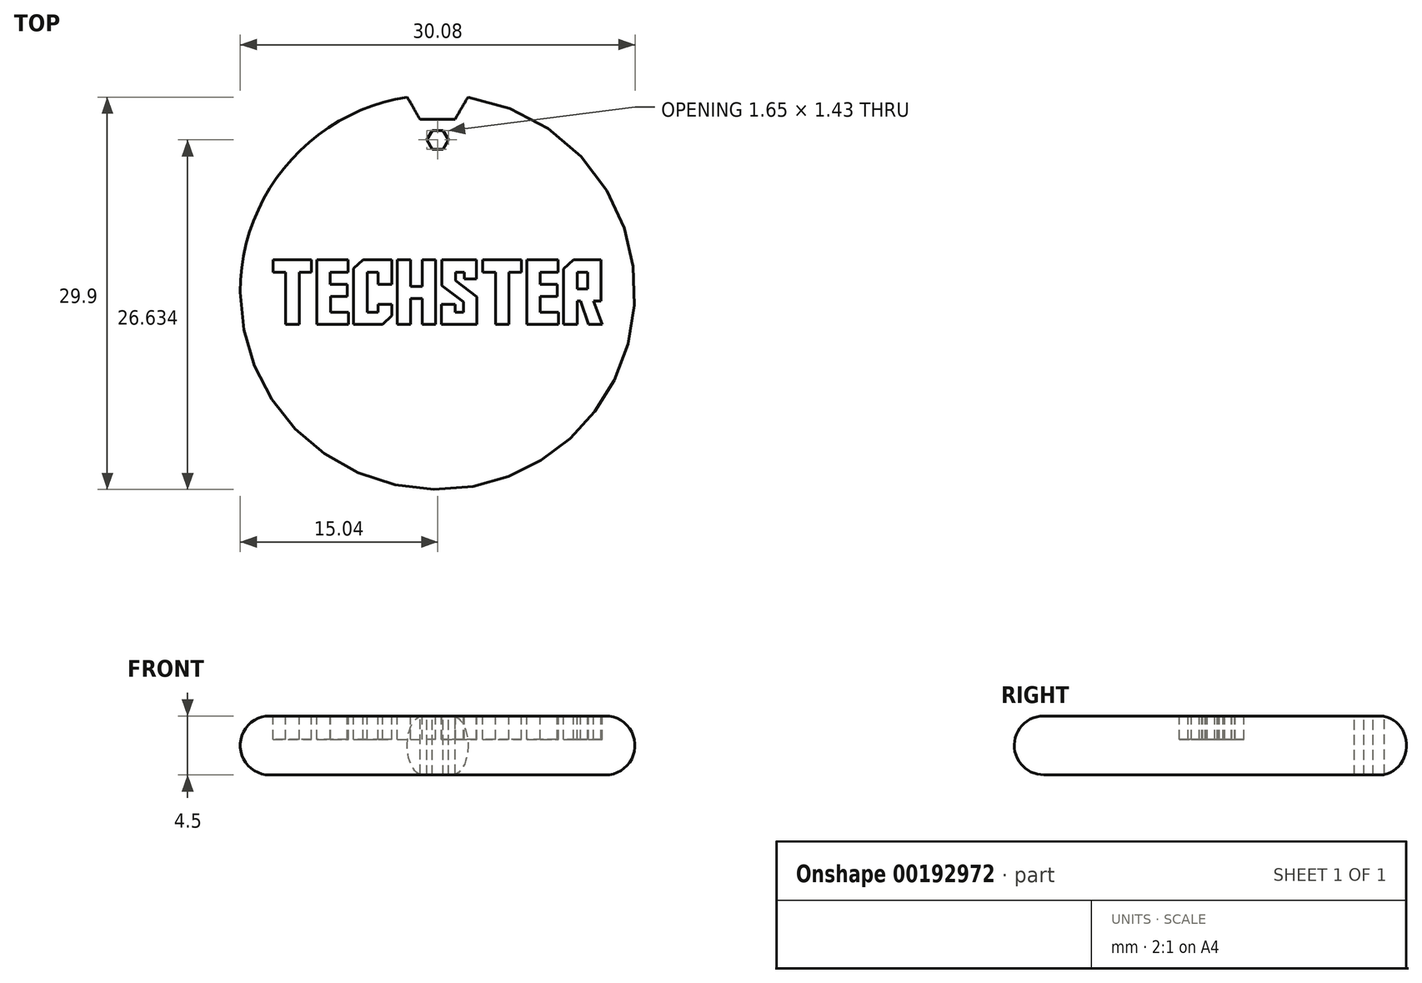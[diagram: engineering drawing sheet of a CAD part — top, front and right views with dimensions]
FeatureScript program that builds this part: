
annotation { "Feature Type Name" : "Feature", "Feature Type Description" : "" }
export const myFeature = defineFeature(function(context is Context, id is Id, definition is map)
    precondition{}
    {
        {
            var Q0;
            Q0=qCreatedBy(makeId("Front.planeOp"),FACE);
            var sketch = newSketch(context, id + "F0", { "sketchPlane" : qUnion([Q0])});
            skLineSegment(sketch, "E0.bottom", {"start": v(0, 0) * mm, "end": v(-12.79, 0) * mm});
            skLineSegment(sketch, "E0.top", {"start": v(0, 4.5) * mm, "end": v(-12.79, 4.5) * mm});
            skLineSegment(sketch, "E0.left", {"start": v(0, 0) * mm, "end": v(0, 4.5) * mm});
            skLineSegment(sketch, "E0.right", {"start": v(-12.79, 0) * mm, "end": v(-12.79, 4.5) * mm});
            skArc(sketch, "E1", {"start": v(-12.79, 4.5) * mm, "mid": v(-15.04, 2.25) * mm, "end": v(-12.79, 0) * mm});
            skSolve(sketch);
        }
        {
            var Q0;
            Q0 = qSketchRegion(id + "F0", true);
            var Q1;
            Q1=sQuery(id+"F0.wireOp",EDGE,"E0.left");
            revolve(context, id + "F1", {"entities" : qUnion([Q0]), "axis" : qUnion([Q1]), "revolveType" : RevolveType.FULL});
        }
        {
            var Q0;
            Q0=qCreatedBy(makeId("Top.planeOp"),FACE);
            cPlane(context, id + "F2", {"entities" : qUnion([Q0]), "cplaneType" : CPlaneType.OFFSET, "offset" : 7 * mm, "width" : 152.4 * mm, "height" : 152.4 * mm});
        }
        {
            var Q0;
            Q0=qCreatedBy(id+"F2.planeOp",FACE);
            var sketch = newSketch(context, id + "F3", { "sketchPlane" : qUnion([Q0])});
            skLineSegment(sketch, "E2", {"start": v(-9.62, 1.52) * mm, "end": v(-10.55, 1.52) * mm});
            skLineSegment(sketch, "E3", {"start": v(-10.55, 1.52) * mm, "end": v(-10.55, -2.46) * mm});
            skLineSegment(sketch, "E4", {"start": v(-10.55, -2.46) * mm, "end": v(-11.58, -2.46) * mm});
            skLineSegment(sketch, "E5", {"start": v(-11.58, -2.46) * mm, "end": v(-11.58, 1.52) * mm});
            skLineSegment(sketch, "E6", {"start": v(-11.58, 1.52) * mm, "end": v(-12.55, 1.52) * mm});
            skLineSegment(sketch, "E7", {"start": v(-12.55, 1.52) * mm, "end": v(-12.55, 2.46) * mm});
            skLineSegment(sketch, "E8", {"start": v(-12.55, 2.46) * mm, "end": v(-9.62, 2.46) * mm});
            skLineSegment(sketch, "E9", {"start": v(-9.62, 2.46) * mm, "end": v(-9.62, 1.52) * mm});
            skLineSegment(sketch, "E10", {"start": v(-9.2, 2.46) * mm, "end": v(-6.81, 2.46) * mm});
            skLineSegment(sketch, "E11", {"start": v(-6.81, 2.46) * mm, "end": v(-6.81, 1.52) * mm});
            skLineSegment(sketch, "E12", {"start": v(-6.81, 1.52) * mm, "end": v(-8.18, 1.52) * mm});
            skLineSegment(sketch, "E13", {"start": v(-8.18, 1.52) * mm, "end": v(-8.18, 0.58) * mm});
            skLineSegment(sketch, "E14", {"start": v(-8.18, 0.58) * mm, "end": v(-6.88, 0.58) * mm});
            skLineSegment(sketch, "E15", {"start": v(-6.88, 0.58) * mm, "end": v(-6.88, -0.34) * mm});
            skLineSegment(sketch, "E16", {"start": v(-6.88, -0.34) * mm, "end": v(-8.16, -0.34) * mm});
            skLineSegment(sketch, "E17", {"start": v(-8.16, -0.34) * mm, "end": v(-8.16, -1.53) * mm});
            skLineSegment(sketch, "E18", {"start": v(-8.16, -1.53) * mm, "end": v(-6.78, -1.53) * mm});
            skLineSegment(sketch, "E19", {"start": v(-6.78, -1.53) * mm, "end": v(-6.78, -2.46) * mm});
            skLineSegment(sketch, "E20", {"start": v(-6.78, -2.46) * mm, "end": v(-9.2, -2.46) * mm});
            skLineSegment(sketch, "E21", {"start": v(-9.2, -2.46) * mm, "end": v(-9.2, 2.46) * mm});
            skLineSegment(sketch, "E22", {"start": v(-4.53, -1.53) * mm, "end": v(-4.53, -0.93) * mm});
            skLineSegment(sketch, "E23", {"start": v(-4.53, -0.93) * mm, "end": v(-3.5, -0.93) * mm});
            skLineSegment(sketch, "E24", {"start": v(-3.5, -0.93) * mm, "end": v(-3.5, -1.78) * mm});
            skLineSegment(sketch, "E25", {"start": v(-3.5, -1.78) * mm, "end": v(-4.18, -2.46) * mm});
            skLineSegment(sketch, "E26", {"start": v(-4.18, -2.46) * mm, "end": v(-6.4, -2.46) * mm});
            skLineSegment(sketch, "E27", {"start": v(-6.4, -2.46) * mm, "end": v(-6.4, 1.78) * mm});
            skLineSegment(sketch, "E28", {"start": v(-6.4, 1.78) * mm, "end": v(-5.66, 2.46) * mm});
            skLineSegment(sketch, "E29", {"start": v(-5.66, 2.46) * mm, "end": v(-3.5, 2.46) * mm});
            skLineSegment(sketch, "E30", {"start": v(-3.5, 2.46) * mm, "end": v(-3.5, 0.6) * mm});
            skLineSegment(sketch, "E31", {"start": v(-3.5, 0.6) * mm, "end": v(-4.53, 0.6) * mm});
            skLineSegment(sketch, "E32", {"start": v(-4.53, 0.6) * mm, "end": v(-4.53, 1.52) * mm});
            skLineSegment(sketch, "E33", {"start": v(-4.53, 1.52) * mm, "end": v(-5.36, 1.52) * mm});
            skLineSegment(sketch, "E34", {"start": v(-5.36, 1.52) * mm, "end": v(-5.36, -1.53) * mm});
            skLineSegment(sketch, "E35", {"start": v(-5.36, -1.53) * mm, "end": v(-4.53, -1.53) * mm});
            skLineSegment(sketch, "E36", {"start": v(-2.06, 0.44) * mm, "end": v(-1.17, 0.44) * mm});
            skLineSegment(sketch, "E37", {"start": v(-1.17, 0.44) * mm, "end": v(-1.17, 2.46) * mm});
            skLineSegment(sketch, "E38", {"start": v(-1.17, 2.46) * mm, "end": v(-0.14, 2.46) * mm});
            skLineSegment(sketch, "E39", {"start": v(-0.14, 2.46) * mm, "end": v(-0.14, -2.46) * mm});
            skLineSegment(sketch, "E40", {"start": v(-0.14, -2.46) * mm, "end": v(-1.17, -2.46) * mm});
            skLineSegment(sketch, "E41", {"start": v(-1.17, -2.46) * mm, "end": v(-1.17, -0.5) * mm});
            skLineSegment(sketch, "E42", {"start": v(-1.17, -0.5) * mm, "end": v(-2.06, -0.5) * mm});
            skLineSegment(sketch, "E43", {"start": v(-2.06, -0.5) * mm, "end": v(-2.06, -2.46) * mm});
            skLineSegment(sketch, "E44", {"start": v(-2.06, -2.46) * mm, "end": v(-3.09, -2.46) * mm});
            skLineSegment(sketch, "E45", {"start": v(-3.09, -2.46) * mm, "end": v(-3.09, 2.46) * mm});
            skLineSegment(sketch, "E46", {"start": v(-3.09, 2.46) * mm, "end": v(-2.06, 2.46) * mm});
            skLineSegment(sketch, "E47", {"start": v(-2.06, 2.46) * mm, "end": v(-2.06, 0.44) * mm});
            skLineSegment(sketch, "E48", {"start": v(3, -2.46) * mm, "end": v(0.3, -2.46) * mm});
            skLineSegment(sketch, "E49", {"start": v(0.3, -2.46) * mm, "end": v(0.3, -0.93) * mm});
            skLineSegment(sketch, "E50", {"start": v(0.3, -0.93) * mm, "end": v(1.33, -0.93) * mm});
            skLineSegment(sketch, "E51", {"start": v(1.33, -0.93) * mm, "end": v(1.33, -1.53) * mm});
            skLineSegment(sketch, "E52", {"start": v(1.33, -1.53) * mm, "end": v(1.97, -1.53) * mm});
            skLineSegment(sketch, "E53", {"start": v(1.97, -1.53) * mm, "end": v(1.97, -0.75) * mm});
            skLineSegment(sketch, "E54", {"start": v(1.97, -0.75) * mm, "end": v(0.33, 0.49) * mm});
            skLineSegment(sketch, "E55", {"start": v(0.33, 0.49) * mm, "end": v(0.33, 2.46) * mm});
            skLineSegment(sketch, "E56", {"start": v(0.33, 2.46) * mm, "end": v(2.97, 2.46) * mm});
            skLineSegment(sketch, "E57", {"start": v(2.97, 2.46) * mm, "end": v(2.97, 1) * mm});
            skLineSegment(sketch, "E58", {"start": v(2.97, 1) * mm, "end": v(2.04, 1) * mm});
            skLineSegment(sketch, "E59", {"start": v(2.04, 1) * mm, "end": v(2.04, 1.52) * mm});
            skLineSegment(sketch, "E60", {"start": v(2.04, 1.52) * mm, "end": v(1.36, 1.52) * mm});
            skLineSegment(sketch, "E61", {"start": v(1.36, 1.52) * mm, "end": v(1.36, 0.88) * mm});
            skLineSegment(sketch, "E62", {"start": v(1.36, 0.88) * mm, "end": v(3, -0.35) * mm});
            skLineSegment(sketch, "E63", {"start": v(3, -0.35) * mm, "end": v(3, -2.46) * mm});
            skLineSegment(sketch, "E64", {"start": v(6.38, 1.52) * mm, "end": v(5.45, 1.52) * mm});
            skLineSegment(sketch, "E65", {"start": v(5.45, 1.52) * mm, "end": v(5.45, -2.46) * mm});
            skLineSegment(sketch, "E66", {"start": v(5.45, -2.46) * mm, "end": v(4.41, -2.46) * mm});
            skLineSegment(sketch, "E67", {"start": v(4.41, -2.46) * mm, "end": v(4.41, 1.52) * mm});
            skLineSegment(sketch, "E68", {"start": v(4.41, 1.52) * mm, "end": v(3.45, 1.52) * mm});
            skLineSegment(sketch, "E69", {"start": v(3.45, 1.52) * mm, "end": v(3.45, 2.46) * mm});
            skLineSegment(sketch, "E70", {"start": v(3.45, 2.46) * mm, "end": v(6.38, 2.46) * mm});
            skLineSegment(sketch, "E71", {"start": v(6.38, 2.46) * mm, "end": v(6.38, 1.52) * mm});
            skLineSegment(sketch, "E72", {"start": v(6.8, 2.46) * mm, "end": v(9.19, 2.46) * mm});
            skLineSegment(sketch, "E73", {"start": v(9.19, 2.46) * mm, "end": v(9.19, 1.52) * mm});
            skLineSegment(sketch, "E74", {"start": v(9.19, 1.52) * mm, "end": v(7.82, 1.52) * mm});
            skLineSegment(sketch, "E75", {"start": v(7.82, 1.52) * mm, "end": v(7.82, 0.58) * mm});
            skLineSegment(sketch, "E76", {"start": v(7.82, 0.58) * mm, "end": v(9.12, 0.58) * mm});
            skLineSegment(sketch, "E77", {"start": v(9.12, 0.58) * mm, "end": v(9.12, -0.34) * mm});
            skLineSegment(sketch, "E78", {"start": v(9.12, -0.34) * mm, "end": v(7.83, -0.34) * mm});
            skLineSegment(sketch, "E79", {"start": v(7.83, -0.34) * mm, "end": v(7.83, -1.53) * mm});
            skLineSegment(sketch, "E80", {"start": v(7.83, -1.53) * mm, "end": v(9.22, -1.53) * mm});
            skLineSegment(sketch, "E81", {"start": v(9.22, -1.53) * mm, "end": v(9.22, -2.46) * mm});
            skLineSegment(sketch, "E82", {"start": v(9.22, -2.46) * mm, "end": v(6.8, -2.46) * mm});
            skLineSegment(sketch, "E83", {"start": v(6.8, -2.46) * mm, "end": v(6.8, 2.46) * mm});
            skLineSegment(sketch, "E84", {"start": v(11.51, -2.46) * mm, "end": v(10.9, -0.68) * mm});
            skLineSegment(sketch, "E85", {"start": v(10.9, -0.68) * mm, "end": v(10.63, -0.68) * mm});
            skLineSegment(sketch, "E86", {"start": v(10.63, -0.68) * mm, "end": v(10.63, -2.46) * mm});
            skLineSegment(sketch, "E87", {"start": v(10.63, -2.46) * mm, "end": v(9.6, -2.46) * mm});
            skLineSegment(sketch, "E88", {"start": v(9.6, -2.46) * mm, "end": v(9.6, 1.77) * mm});
            skLineSegment(sketch, "E89", {"start": v(9.6, 1.77) * mm, "end": v(10.35, 2.46) * mm});
            skLineSegment(sketch, "E90", {"start": v(10.35, 2.46) * mm, "end": v(12.45, 2.46) * mm});
            skLineSegment(sketch, "E91", {"start": v(12.45, 2.46) * mm, "end": v(12.45, -0.67) * mm});
            skLineSegment(sketch, "E92", {"start": v(12.45, -0.67) * mm, "end": v(11.9, -0.67) * mm});
            skLineSegment(sketch, "E93", {"start": v(11.9, -0.67) * mm, "end": v(12.55, -2.46) * mm});
            skLineSegment(sketch, "E94", {"start": v(12.55, -2.46) * mm, "end": v(11.51, -2.46) * mm});
            skLineSegment(sketch, "E95", {"start": v(11.42, 0.24) * mm, "end": v(11.42, 1.52) * mm});
            skLineSegment(sketch, "E96", {"start": v(11.42, 1.52) * mm, "end": v(10.63, 1.52) * mm});
            skLineSegment(sketch, "E97", {"start": v(10.63, 1.52) * mm, "end": v(10.63, 0.24) * mm});
            skLineSegment(sketch, "E98", {"start": v(10.63, 0.24) * mm, "end": v(11.42, 0.24) * mm});
            skSolve(sketch);
        }
        {
            var Q0;
            Q0 = qSketchRegion(id + "F3", true);
            extrude(context, id + "F4", {"entities" : qUnion([Q0]), "operationType" : NewBodyOperationType.REMOVE, "oppositeDirection" : true, "depth" : 4.3 * mm});
        }
        {
            var Q0;
            Q0=qCreatedBy(id+"F2.planeOp",FACE);
            var sketch = newSketch(context, id + "F5", { "sketchPlane" : qUnion([Q0])});
            skCircle(sketch, "E99.cCircle", {"center": v(0, 15.5) * mm, "radius": 2.32 * mm, "construction": true});
            skLineSegment(sketch, "E99.0", {"start": v(1.34, 13.17) * mm, "end": v(-1.34, 13.17) * mm});
            skLineSegment(sketch, "E99.1", {"start": v(-1.34, 13.17) * mm, "end": v(-2.68, 15.5) * mm});
            skLineSegment(sketch, "E99.2", {"start": v(-2.68, 15.5) * mm, "end": v(-1.34, 17.82) * mm});
            skLineSegment(sketch, "E99.3", {"start": v(-1.34, 17.82) * mm, "end": v(1.34, 17.82) * mm});
            skLineSegment(sketch, "E99.4", {"start": v(1.34, 17.82) * mm, "end": v(2.68, 15.5) * mm});
            skLineSegment(sketch, "E99.5", {"start": v(2.68, 15.5) * mm, "end": v(1.34, 13.17) * mm});
            skPoint(sketch, "E99.0.midPoint", {"position": v(0, 13.17) * mm});
            skSolve(sketch);
        }
        {
            var Q0;
            Q0=makeQuery(id+"F5.imprint","IMPRINT",FACE,{"disambiguationData":[TD([[makeQuery(id+"F5.imprint","IMPRINT",EDGE,{"derivedFrom":sQuery(id+"F5.wireOp",EDGE,"E99.0")}),-1.0]])]});
            extrude(context, id + "F6", {"entities" : qUnion([Q0]), "operationType" : NewBodyOperationType.REMOVE, "oppositeDirection" : true, "depth" : 25.4 * mm});
        }
        {
            var Q0;
            Q0=qCreatedBy(id+"F2.planeOp",FACE);
            var sketch = newSketch(context, id + "F7", { "sketchPlane" : qUnion([Q0])});
            skCircle(sketch, "E100.cCircle", {"center": v(0, 11.6) * mm, "radius": 0.71 * mm, "construction": true});
            skLineSegment(sketch, "E100.0", {"start": v(0.41, 10.88) * mm, "end": v(-0.41, 10.88) * mm});
            skLineSegment(sketch, "E100.1", {"start": v(-0.41, 10.88) * mm, "end": v(-0.82, 11.6) * mm});
            skLineSegment(sketch, "E100.2", {"start": v(-0.82, 11.6) * mm, "end": v(-0.41, 12.3) * mm});
            skLineSegment(sketch, "E100.3", {"start": v(-0.41, 12.3) * mm, "end": v(0.41, 12.3) * mm});
            skLineSegment(sketch, "E100.4", {"start": v(0.41, 12.3) * mm, "end": v(0.82, 11.6) * mm});
            skLineSegment(sketch, "E100.5", {"start": v(0.82, 11.6) * mm, "end": v(0.41, 10.88) * mm});
            skPoint(sketch, "E100.0.midPoint", {"position": v(0, 10.88) * mm});
            skSolve(sketch);
        }
        {
            var Q0;
            Q0 = qSketchRegion(id + "F7", true);
            extrude(context, id + "F8", {"entities" : qUnion([Q0]), "operationType" : NewBodyOperationType.REMOVE, "oppositeDirection" : true, "depth" : 25.4 * mm});
        }
    });
